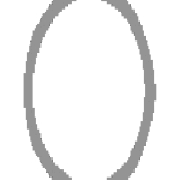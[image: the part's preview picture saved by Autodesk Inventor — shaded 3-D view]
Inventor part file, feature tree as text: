
AUTODESK INVENTOR PART (.ipt)
format: ipt  version: 2021 (Build 250183000, 183)  size: 112,128 bytes
history: native  units: in
note: dims shown in document units (in); Inventor stores cm internally (conversion verified against a paired STEP export)
features: other x4, sketch x3, plane x1
ambient origin geometry x8: Origin, YZ Plane, XZ Plane, XY Plane, X Axis, Y Axis, Z Axis, Center Point
bodies: Solid1 (feature_tree), Body (feature_tree)
feature tree (8):
  other  "Driven Length"
  other  "Frame Generator"
  other  "Start Plane"
  other  "End Plane"
  sketch  "Sketch"  dims[d2=21.1542in d4=-0.0in d5=21.1542in d6=0.12in d7=0.0in d8=90.0deg d9=21.1542in]
  sketch  "Sketch2"  dims[d0=1.0in]
  plane  "Work Plane3"
  sketch  "Sketch3"  dims[d1=0.065in]
